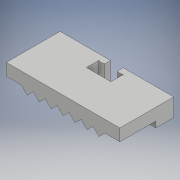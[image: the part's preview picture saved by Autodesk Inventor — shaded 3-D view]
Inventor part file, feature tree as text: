
AUTODESK INVENTOR PART (.ipt)
format: ipt  version: 2017 (Build 210142000, 142)  size: 220,672 bytes
history: native  units: mm
features: extrude x6, sketch x5, chamfer x1
ambient origin geometry x8: Origin, YZ Plane, XZ Plane, XY Plane, X Axis, Y Axis, Z Axis, Center Point
bodies: Solid1 (feature_tree)
feature tree (12):
  extrude  "Extrusion1"  Depth=9.0mm
  extrude  "Extrusion8"  Depth=1.0mm
  extrude  "Extrusion10"  TaperAngle=135.0deg  [1 undecoded]
  extrude  "Extrusion12"  Depth=4.0mm TaperAngle=0.0deg
  chamfer  "Chamfer1"  Distance=4.1mm
  extrude  "Extrusion13"  Depth=2.1mm
  extrude  "Extrusion14"  Depth=2.1mm
  sketch  "Sketch1"  dims[d0=19.0mm d1=9.0mm]
  sketch  "Sketch12"  dims[d2=3.0mm d3=0.0mm d23=1.0mm]
  sketch  "Sketch14"  dims[d24=6.0mm d25=135.0deg]
  sketch  "Sketch16"  dims[d26=90.0deg d27=4.0mm d28=0.0mm]
  sketch  "Sketch18"  dims[d47=2.0mm d48=4.1mm d49=2.1mm d50=2.1mm d51=10.0mm d52=0.0mm d57=6.0mm d58=1.0mm d59=3.5mm d60=1.0mm d61=0.0mm d62=0.5mm d63=2.0mm d64=45.0deg d66=1.0mm d67=1.0mm d68=10.0mm d69=0.0mm d71=135.0deg d72=90.0deg d73=135.0deg d74=5.0mm d75=0.0mm]
note: 1 required parameter value undecoded (feature->parameter linkage not recoverable at this tier; creation-order binding heuristic only, values carry confidence <= 0.55)
